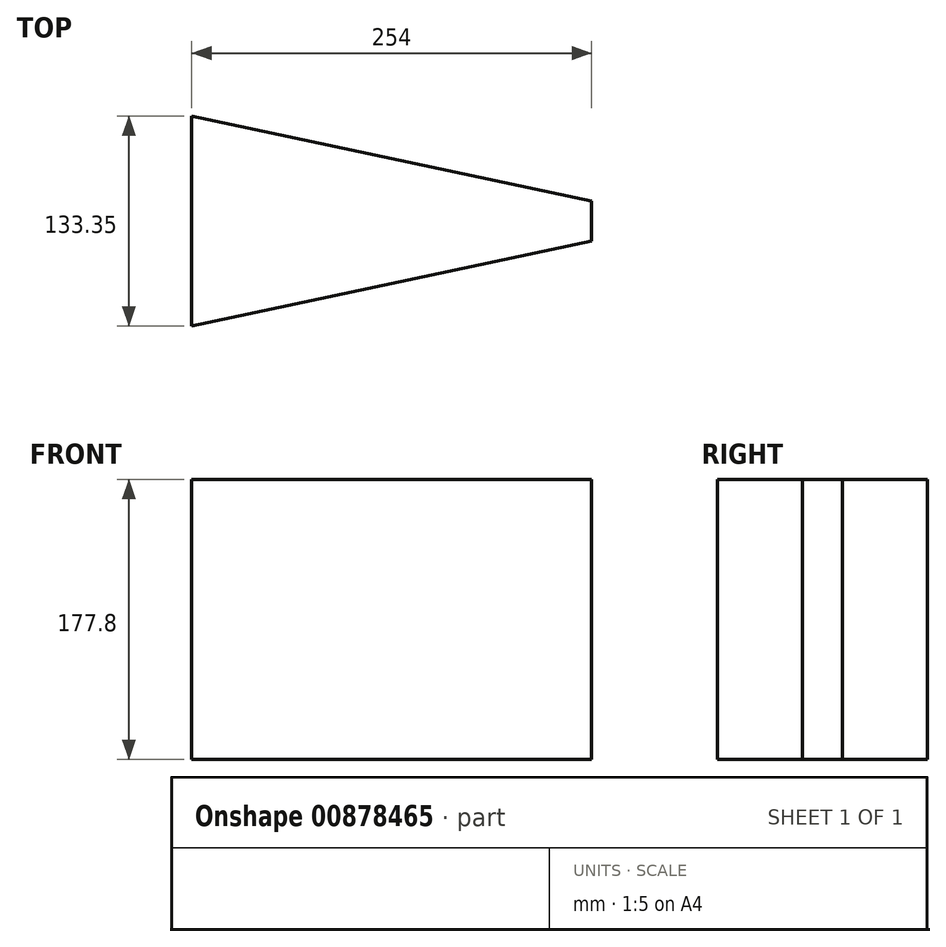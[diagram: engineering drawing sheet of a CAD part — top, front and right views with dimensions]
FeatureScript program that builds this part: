
annotation { "Feature Type Name" : "Feature", "Feature Type Description" : "" }
export const myFeature = defineFeature(function(context is Context, id is Id, definition is map)
    precondition{}
    {
        {
            var Q0;
            Q0=qCreatedBy(makeId("Top.planeOp"),FACE);
            var sketch = newSketch(context, id + "F0", { "sketchPlane" : qUnion([Q0])});
            skLineSegment(sketch, "E0.left", {"start": v(201.64, 11.3) * mm, "end": v(201.64, -14.1) * mm});
            skLineSegment(sketch, "E0.right", {"start": v(-52.36, 65.27) * mm, "end": v(-52.36, -68.08) * mm});
            skLineSegment(sketch, "E1", {"start": v(-52.36, 65.27) * mm, "end": v(201.64, 11.3) * mm});
            skLineSegment(sketch, "E2", {"start": v(201.64, -14.1) * mm, "end": v(-52.36, -68.08) * mm});
            skPoint(sketch, "E0.bottom.start.orphan", {"position": v(201.64, 65.27) * mm});
            skPoint(sketch, "E0.top.start.orphan", {"position": v(201.64, -68.08) * mm});
            skPoint(sketch, "E3.end.orphan", {"position": v(201.64, -1.4) * mm});
            skPoint(sketch, "E3.start.orphan", {"position": v(-52.36, -1.4) * mm});
            skSolve(sketch);
        }
        {
            var Q0;
            Q0 = qSketchRegion(id + "F0", true);
            extrude(context, id + "F1", {"entities" : qUnion([Q0]), "depth" : 177.8 * mm, "offsetDistance" : 25.4 * mm});
        }
    });
